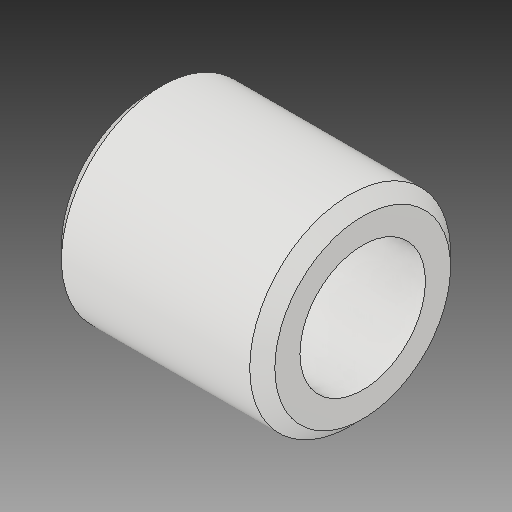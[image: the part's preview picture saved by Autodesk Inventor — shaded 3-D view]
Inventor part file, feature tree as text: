
AUTODESK INVENTOR PART (.ipt)
format: ipt  version: 2019 (Build 230136000, 136)  size: 110,080 bytes
history: native  units: in
note: dims shown in document units (in); Inventor stores cm internally (conversion verified against a paired STEP export)
features: chamfer x1
ambient origin geometry x8: Origin, YZ Plane, XZ Plane, XY Plane, X Axis, Y Axis, Z Axis, Center Point
bodies: Solid1 (feature_tree)
feature tree (1):
  chamfer  "Chamfer1"  [1 undecoded]
note: 1 required parameter value undecoded (feature->parameter linkage not recoverable at this tier; creation-order binding heuristic only, values carry confidence <= 0.55)
